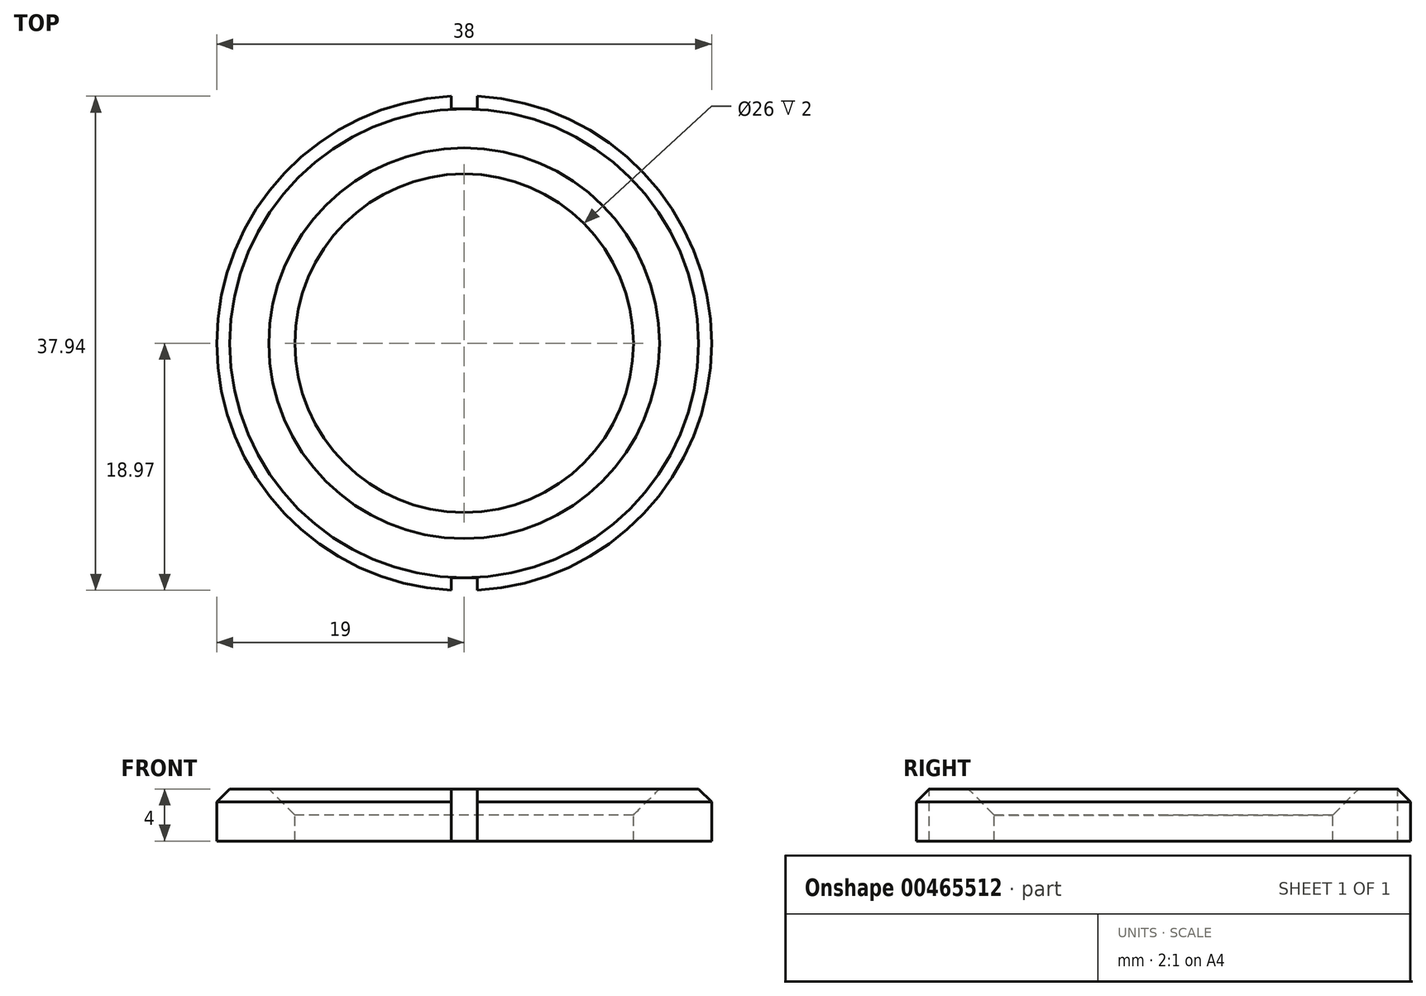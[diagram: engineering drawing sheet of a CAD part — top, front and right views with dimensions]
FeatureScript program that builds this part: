
annotation { "Feature Type Name" : "Feature", "Feature Type Description" : "" }
export const myFeature = defineFeature(function(context is Context, id is Id, definition is map)
    precondition{}
    {
        {
            var Q0;
            Q0=qCreatedBy(makeId("Top.planeOp"),FACE);
            var sketch = newSketch(context, id + "F0", { "sketchPlane" : qUnion([Q0])});
            skCircle(sketch, "E0", {"center": v(0, 0) * mm, "radius": 13 * mm});
            skCircle(sketch, "E1", {"center": v(0, 0) * mm, "radius": 19 * mm});
            skSolve(sketch);
        }
        {
            var Q0;
            Q0 = qSketchRegion(id + "F0", true);
            extrude(context, id + "F1", {"entities" : qUnion([Q0]), "oppositeDirection" : true, "depth" : 4 * mm});
        }
        {
            var Q0;
            Q0=makeQuery(id+"F1.opExtrude","CAP_EDGE",EDGE,{"disambiguationData":[OSD([sQuery(id+"F0.wireOp",EDGE,"E1")])],"isStart":true});
            chamfer(context, id + "F2", {"entities" : qUnion([Q0]), "width" : 1 * mm, "tangentPropagation" : true});
        }
        {
            var Q0;
            Q0=makeQuery(id+"F1.opExtrude","CAP_EDGE",EDGE,{"disambiguationData":[OSD([sQuery(id+"F0.wireOp",EDGE,"E0")])],"isStart":true});
            chamfer(context, id + "F3", {"entities" : qUnion([Q0]), "width" : 2 * mm, "tangentPropagation" : true});
        }
        {
            var Q0;
            Q0=makeQuery(id+"F1.opExtrude","CAP_FACE",FACE,{"disambiguationData":[OSD([sQuery(id+"F0.wireOp",EDGE,"E0"),sQuery(id+"F0.wireOp",EDGE,"E1")])],"isStart":true});
            var sketch = newSketch(context, id + "F4", { "sketchPlane" : qUnion([Q0])});
            skLineSegment(sketch, "E2.bottom", {"start": v(-1, 18) * mm, "end": v(1, 18) * mm});
            skLineSegment(sketch, "E2.top", {"start": v(-1, -18) * mm, "end": v(1, -18) * mm});
            skLineSegment(sketch, "E2.left", {"start": v(-1, 18) * mm, "end": v(-1, -18) * mm});
            skLineSegment(sketch, "E2.right", {"start": v(1, 18) * mm, "end": v(1, -18) * mm});
            skPoint(sketch, "E2.middle", {"position": v(0, 0) * mm});
            skCircle(sketch, "E3.0", {"center": v(0, 0) * mm, "radius": 19 * mm});
            skLineSegment(sketch, "E4", {"start": v(-1, 18) * mm, "end": v(-1, 18.97) * mm});
            skLineSegment(sketch, "E5", {"start": v(1, 18) * mm, "end": v(1, 18.97) * mm});
            skLineSegment(sketch, "E6", {"start": v(-1, -18) * mm, "end": v(-1, -18.97) * mm});
            skLineSegment(sketch, "E7", {"start": v(1, -18) * mm, "end": v(1, -18.97) * mm});
            skSolve(sketch);
        }
        {
            var Q0;
            {var subQ0=sQuery(id+"F4.wireOp",EDGE,"E4");Q0=makeQuery(id+"F4.imprint","IMPRINT",FACE,{"disambiguationData":[TD([[makeQuery(id+"F4.imprint","IMPRINT",EDGE,{"derivedFrom":subQ0}),-1.0]])]});}
            var Q1;
            {var subQ0=sQuery(id+"F4.wireOp",EDGE,"E6");Q1=makeQuery(id+"F4.imprint","IMPRINT",FACE,{"disambiguationData":[TD([[makeQuery(id+"F4.imprint","IMPRINT",EDGE,{"derivedFrom":subQ0}),1.0]])]});}
            extrude(context, id + "F5", {"entities" : qUnion([Q0, Q1]), "operationType" : NewBodyOperationType.REMOVE, "endBound" : BoundingType.THROUGH_ALL, "oppositeDirection" : true, "depth" : 25 * mm});
        }
    });
